# Revit family: KD-Druckhaltung
name_source: partatom
category: HLS-Bauteile
units: mm (PartAtom-declared; Revit-internal decimal feet)

## family parameters
Arbeitsebenenbasiert = Nein
Beim Laden mit Abzugskörper schneiden = Nein
Bemaßung runder Anschluss = Durchmesser verwenden
Beschriftungsausrichtung beibehalten = Nein
Gemeinsam genutzt = Nein
Immer vertikal = Ja
OmniClass-Nummer = 23.75.00.00
OmniClass-Titel = Climate Control (HVAC)
Raumberechnungspunkt = Nein
Teiletyp = Normal

## types (8) — shared parameters
BaseMaterial = Kunststoff schwarz
BodyMaterial = Kunststoff - Weiß
HeadMaterial = Kunststoff - Weiß
TopMaterial = Kunststoff schwarz
zero-valued in all types: Vorgabe-Ansicht

## per-type parameters (varying)
| type | Breite | Höhe | Tiefe |
| AST 100/4 | 560 mm  [stored 1.83727 ft] | 1170 mm | 560 mm  [stored 1.83727 ft] |
| AST 150/4 | 560 mm  [stored 1.83727 ft] | 1460 mm  [stored 4.79003 ft] | 560 mm  [stored 1.83727 ft] |
| AST 200/4 | 560 mm  [stored 1.83727 ft] | 1760 mm  [stored 5.77428 ft] | 560 mm  [stored 1.83727 ft] |
| AST 400/6 | 790 mm  [stored 2.59186 ft] | 1570 mm | 790 mm  [stored 2.59186 ft] |
| AST 600/6 | 1020 mm  [stored 3.34646 ft] | 1450 mm  [stored 4.75722 ft] | 1020 mm  [stored 3.34646 ft] |
| AST 1200/6 | 1020 mm  [stored 3.34646 ft] | 1880 mm  [stored 6.16798 ft] | 1020 mm  [stored 3.34646 ft] |
| AST 1600/6 | 1020 mm  [stored 3.34646 ft] | 2380 mm  [stored 7.8084 ft] | 1020 mm  [stored 3.34646 ft] |
| AST 2400/6 | 1350 mm  [stored 4.42913 ft] | 2400 mm | 1350 mm  [stored 4.42913 ft] |

note: [stored X ft] marks values corroborated as IEEE doubles in the binary element streams (Revit-internal decimal feet)

## geometry (parser evidence)
native form markers: Blend x6
no freeform markers — native parametric forms only
